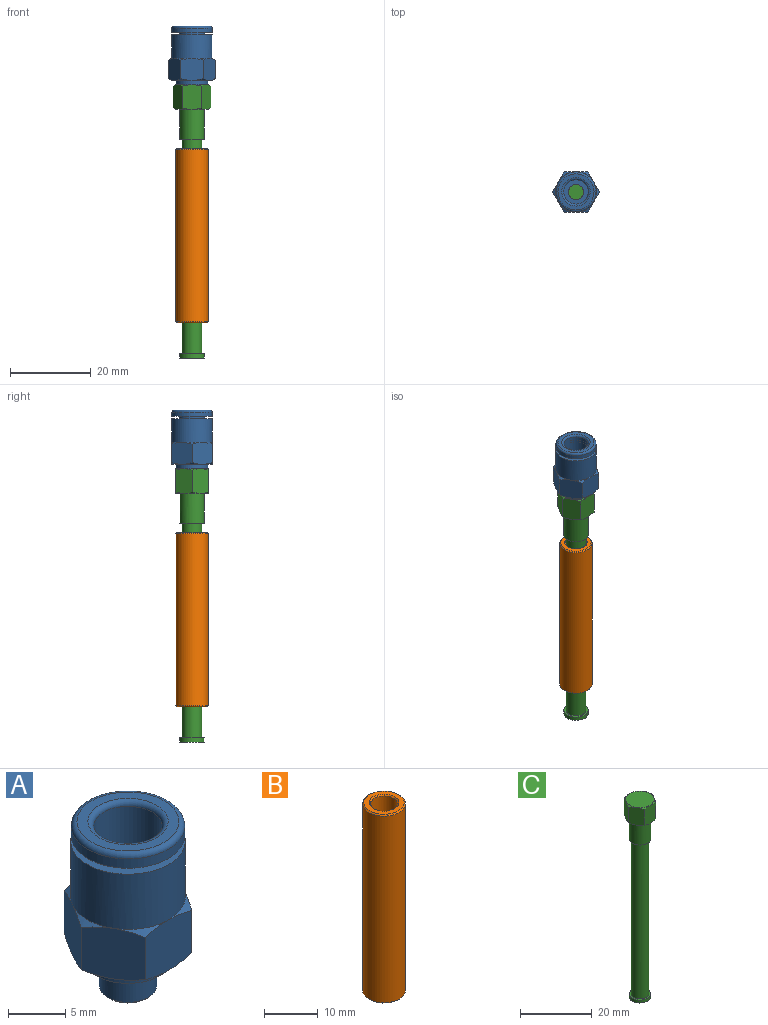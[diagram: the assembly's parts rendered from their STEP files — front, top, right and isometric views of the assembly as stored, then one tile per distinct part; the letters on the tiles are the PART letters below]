
ASSEMBLY  parts=3 mates=2
PART A: 35 faces, bbox 12x12x18.3 mm
  f0: cylinder r=1.88mm len=4.3mm, axis (0,0,1), area 50.7mm2, adj f33,f34
  f1: torus R=3.5mm, axis (0,0,1), area 15.7mm2, adj f2,f11
  f2: cylinder r=3mm len=13mm, axis (0,0,1), area 245mm2, adj f1,f34
  f3: cone r=2.5mm half-angle=45deg, axis (0,0,1), area 5.3mm2, adj f4,f33
  f4: cylinder r=2.5mm len=5mm, axis (0,0,1), area 47.9mm2, adj f3,f32
  f5: cylinder r=3.95mm len=7.9mm, axis (0,0,1), area 27.3mm2, adj f31,f32
  f6: cylinder r=5mm len=10mm, axis (0,0,1), area 185.4mm2, adj f12,f13,f14,f15,f16,f17,f18
  f7: torus R=4.45mm, axis (0,0,1), area 23.5mm2, adj f8,f11
  f8: cylinder r=4.95mm len=9.9mm, axis (0,0,1), area 31.1mm2, adj f7,f10
  f9: cylinder r=3.15mm len=6.3mm, axis (0,0,1), area 11.9mm2, adj f10,f12
  f10: plane 9.9x9.9mm, normal (0,0,-1), area 45.8mm2, adj f8,f9
  f11: plane 8.9x8.9mm, normal (0,0,1), area 23.7mm2, adj f1,f7
  f12: plane 10x10mm, normal (0,0,1), area 47.4mm2, adj f6,f9
  f13: cone r=8mm half-angle=60deg, axis (0,0,-1), area 2.5mm2, adj f6,f19,f20
  f14: cone r=8mm half-angle=60deg, axis (0,0,-1), area 2.5mm2, adj f6,f19,f24
  f15: cone r=8mm half-angle=60deg, axis (0,0,-1), area 2.5mm2, adj f6,f20,f21
  f16: cone r=8mm half-angle=60deg, axis (0,0,-1), area 2.5mm2, adj f6,f21,f22
  f17: cone r=8mm half-angle=60deg, axis (0,0,-1), area 2.5mm2, adj f6,f22,f23
  f18: cone r=8mm half-angle=60deg, axis (0,0,-1), area 2.5mm2, adj f6,f23,f24
  f19: plane 6.25x5.88mm, normal (0,1,0), area 29.4mm2, adj f13,f14,f20,f24,f26,f30
  f20: plane 5.87x5.47mm, normal (-0.87,0.5,0), area 29.4mm2, adj f13,f15,f19,f21,f29,f30
  f21: plane 5.87x5.47mm, normal (-0.87,-0.5,0), area 29.4mm2, adj f15,f16,f20,f22,f28,f29
  f22: plane 6.25x5.88mm, normal (0,-1,0), area 29.4mm2, adj f16,f17,f21,f23,f27,f28
  f23: plane 5.87x5.47mm, normal (0.87,-0.5,0), area 29.4mm2, adj f17,f18,f22,f24,f25,f27
  f24: plane 5.87x5.47mm, normal (0.87,0.5,0), area 29.4mm2, adj f14,f18,f19,f23,f25,f26
  f25: cone r=5mm half-angle=60deg, axis (0,0,1), area 2.5mm2, adj f23,f24,f31
  f26: cone r=5mm half-angle=60deg, axis (0,0,1), area 2.5mm2, adj f19,f24,f31
  f27: cone r=5mm half-angle=60deg, axis (0,0,1), area 2.5mm2, adj f22,f23,f31
  f28: cone r=5mm half-angle=60deg, axis (0,0,1), area 2.5mm2, adj f21,f22,f31
  f29: cone r=5mm half-angle=60deg, axis (0,0,1), area 2.5mm2, adj f20,f21,f31
  f30: cone r=5mm half-angle=60deg, axis (0,0,1), area 2.5mm2, adj f19,f20,f31
  f31: plane 10x10mm, normal (0,0,-1), area 29.5mm2, adj f5,f25,f26,f27,f28,f29,f30
  f32: plane 7.9x7.9mm, normal (0,0,-1), area 29.4mm2, adj f4,f5
  f33: plane 4.5x4.5mm, normal (0,0,-1), area 4.9mm2, adj f0,f3
  f34: plane 6x6mm, normal (0,0,1), area 17.2mm2, adj f0,f2
PART B: 8 faces, bbox 8x8x43 mm
  f0: cone r=2.5mm half-angle=45deg, axis (0,0,-1), area 5.8mm2, adj f4,f7
  f1: cone r=2.5mm half-angle=45deg, axis (0,0,1), area 5.8mm2, adj f4,f6
  f2: cone r=3.75mm half-angle=45deg, axis (0,0,1), area 8.6mm2, adj f5,f7
  f3: cone r=3.75mm half-angle=45deg, axis (0,0,-1), area 8.6mm2, adj f5,f6
  f4: cylinder r=2.5mm len=42.5mm, axis (0,0,1), area 667.6mm2, adj f0,f1
  f5: cylinder r=4mm len=42.5mm, axis (0,0,1), area 1068.1mm2, adj f2,f3
  f6: plane 7.5x7.5mm, normal (0,0,1), area 20.4mm2, adj f1,f3
  f7: plane 7.5x7.5mm, normal (0,0,-1), area 20.4mm2, adj f0,f2
PART C: 26 faces, bbox 9.6x9.6x67.9 mm
  f0: cylinder r=3mm len=6mm, axis (0,0,-1), area 18.8mm2, adj f24,f25
  f1: cylinder r=3mm len=7.4mm, axis (0,0,1), area 139.5mm2, adj f3,f23
  f2: cylinder r=2.45mm len=53mm, axis (0,0,1), area 815.9mm2, adj f3,f24
  f3: plane 6x6mm, normal (0,0,-1), area 9.4mm2, adj f1,f2
  f4: plane 6.48x4.38mm, normal (0.87,-0.5,0), area 27mm2, adj f5,f9,f11,f12,f18,f19
  f5: plane 6.48x5mm, normal (0,-1,0), area 27mm2, adj f4,f6,f12,f13,f19,f20
  f6: plane 6.48x4.38mm, normal (-0.87,-0.5,0), area 27mm2, adj f5,f7,f13,f14,f20,f21
  f7: plane 6.48x4.38mm, normal (-0.87,0.5,0), area 27mm2, adj f6,f8,f14,f15,f21,f22
  f8: plane 6.48x5mm, normal (0,1,0), area 27mm2, adj f7,f9,f10,f15,f17,f22
  f9: plane 6.48x4.38mm, normal (0.87,0.5,0), area 27mm2, adj f4,f8,f10,f11,f17,f18
  f10: cone r=4.62mm half-angle=60deg, axis (0,0,-1), area 1.6mm2, adj f8,f9,f16
  f11: cone r=4.62mm half-angle=60deg, axis (0,0,-1), area 1.6mm2, adj f4,f9,f16
  f12: cone r=4.62mm half-angle=60deg, axis (0,0,-1), area 1.6mm2, adj f4,f5,f16
  f13: cone r=4.62mm half-angle=60deg, axis (0,0,-1), area 1.6mm2, adj f5,f6,f16
  f14: cone r=4.62mm half-angle=60deg, axis (0,0,-1), area 1.6mm2, adj f6,f7,f16
  f15: cone r=4.62mm half-angle=60deg, axis (0,0,-1), area 1.6mm2, adj f7,f8,f16
  f16: plane 8x8mm, normal (0,0,1), area 50.3mm2, adj f10,f11,f12,f13,f14,f15
  f17: cone r=4mm half-angle=60deg, axis (0,0,1), area 1.6mm2, adj f8,f9,f23
  f18: cone r=4mm half-angle=60deg, axis (0,0,1), area 1.6mm2, adj f4,f9,f23
  f19: cone r=4mm half-angle=60deg, axis (0,0,1), area 1.6mm2, adj f4,f5,f23
  f20: cone r=4mm half-angle=60deg, axis (0,0,1), area 1.6mm2, adj f5,f6,f23
  f21: cone r=4mm half-angle=60deg, axis (0,0,1), area 1.6mm2, adj f6,f7,f23
  f22: cone r=4mm half-angle=60deg, axis (0,0,1), area 1.6mm2, adj f7,f8,f23
  f23: plane 8x8mm, normal (0,0,-1), area 22mm2, adj f1,f17,f18,f19,f20,f21,f22
  f24: plane 6x6mm, normal (0,0,1), area 9.4mm2, adj f0,f2
  f25: plane 6x6mm, normal (0,0,-1), area 28.3mm2, adj f0
PLACE A t=(-6.54,-20.04,23.85)mm
PLACE B t=(-6.54,-20.04,-6.44)mm
PLACE C t=(-6.54,-20.04,9.35)mm
MATE planar B.f0 <-> C.f0  axis (0,0,1) through (-6.54,-20.04,-6.69)mm
MATE planar A.f0 <-> C.f0  axis (0,0,-1) through (-6.54,-20.04,9.35)mm
